# Revit family: Accessory-Bath_Fan-KOHLER-ATMO-K-34455_1
name_source: partatom
category: Specialty Equipment
units: mm (PartAtom-declared; Revit-internal decimal feet)

## family parameters
Cut with Voids When Loaded = No
Host = Face
OmniClass Number = 23.31.25.00
OmniClass Title = Toilet and Bath Specialties
Part Type = Normal
Room Calculation Point = No
Round Connector Dimension = Use Diameter
Shared = No

## types (2) — shared parameters
ADA Compliant = No
Apparent Load = 0 VA
Assembly Code = C1030200
Date Modified = 03/02/2023
Default Elevation = 0"
Description = Bath Fan With Light
Electrical Connector = Yes
Electrical Note = One Dedicated Circuit Required
Fan Connector = Yes
Fan Vent Outlet = Fan Vent Outlet
Height = 10 5/8"
Length = 19 13/16"
Manufacturer = Kohler Co.
Master Format 2014 = 10 28 00
Master Format 2014 Name = Toilet, Bath, and Laundry Accessories
Material = Premium Metal Construction
Product Documentation Link = https://www.us.kohler.com
Product Name = ATMO
Product Page URL = http://www.us.kohler.com
URL = https://www.us.kohler.com
Voltage = 120 V
WaterSense Certified = No
Width = 13 7/8"

## per-type parameters (varying)
| type | Finish | Model | Type |
| 0-White | Kohler-Metal-0-White | K-34455-0 | 1 |
| NA-Stainless | Kohler-Metal-NA-Stainless | K-34455-NA | 2 |

## geometry (parser evidence)
native form markers: Sweep x7
no freeform markers — native parametric forms only
